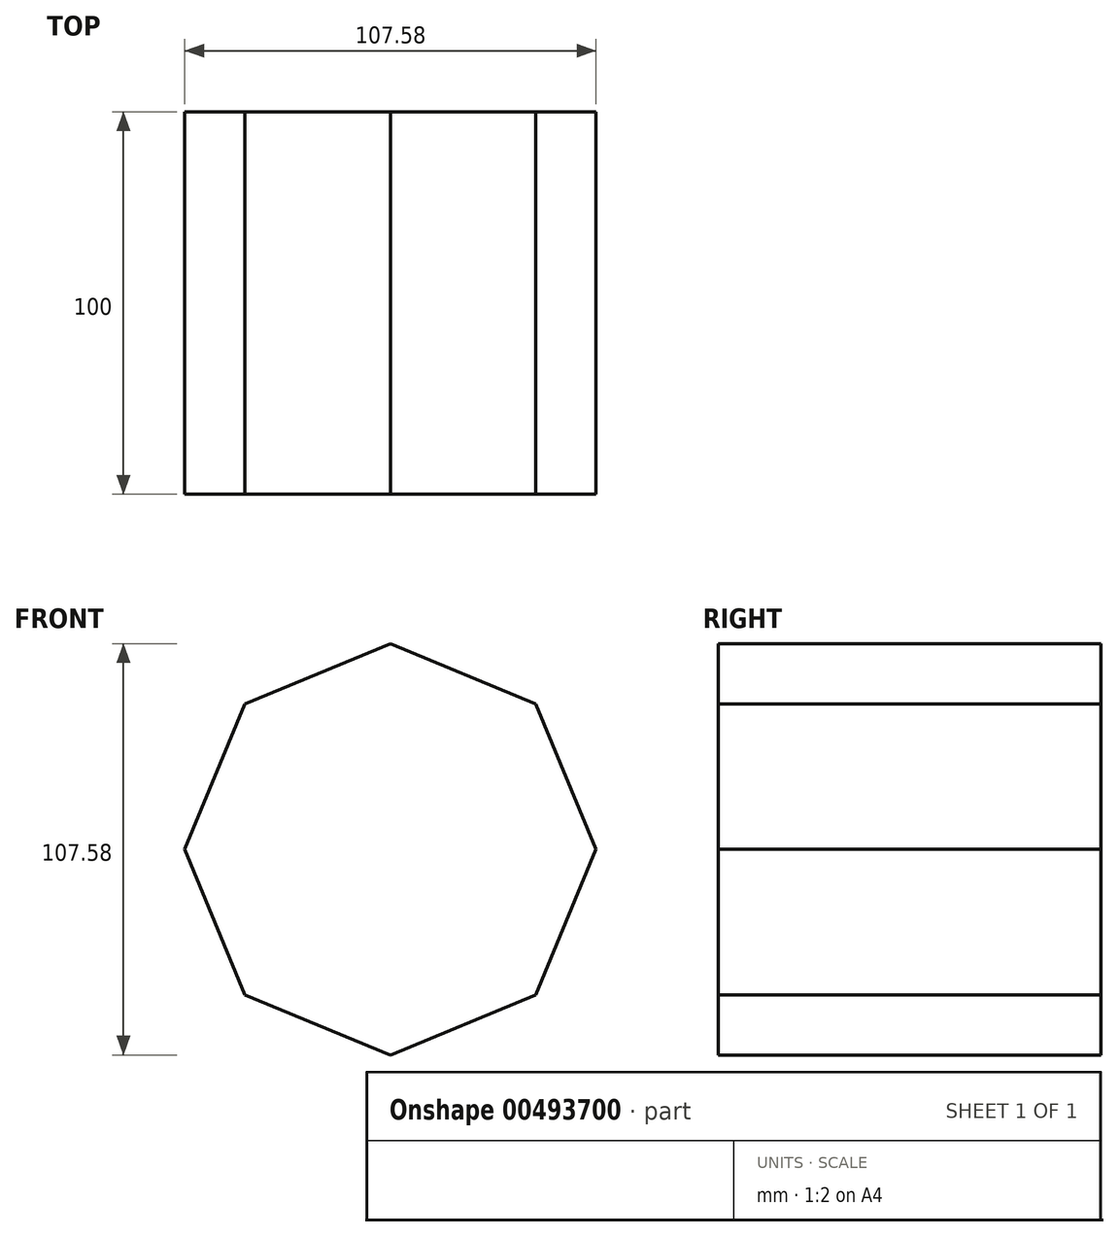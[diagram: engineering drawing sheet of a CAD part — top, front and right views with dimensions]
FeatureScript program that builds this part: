
annotation { "Feature Type Name" : "Feature", "Feature Type Description" : "" }
export const myFeature = defineFeature(function(context is Context, id is Id, definition is map)
    precondition{}
    {
        {
            var Q0;
            Q0=qCreatedBy(makeId("Front.planeOp"),FACE);
            var sketch = newSketch(context, id + "F0", { "sketchPlane" : qUnion([Q0])});
            skCircle(sketch, "E0.cCircle", {"center": v(0, 0) * mm, "radius": 53.8 * mm, "construction": true});
            skLineSegment(sketch, "E0.0", {"start": v(0, 53.8) * mm, "end": v(38.04, 38.04) * mm});
            skLineSegment(sketch, "E0.1", {"start": v(38.04, 38.04) * mm, "end": v(53.8, 0) * mm});
            skLineSegment(sketch, "E0.2", {"start": v(53.8, 0) * mm, "end": v(38.04, -38.04) * mm});
            skLineSegment(sketch, "E0.3", {"start": v(38.04, -38.04) * mm, "end": v(0, -53.8) * mm});
            skLineSegment(sketch, "E0.4", {"start": v(0, -53.8) * mm, "end": v(-38.04, -38.04) * mm});
            skLineSegment(sketch, "E0.5", {"start": v(-38.04, -38.04) * mm, "end": v(-53.8, 0) * mm});
            skLineSegment(sketch, "E0.6", {"start": v(-53.8, 0) * mm, "end": v(-38.04, 38.04) * mm});
            skLineSegment(sketch, "E0.7", {"start": v(-38.04, 38.04) * mm, "end": v(0, 53.8) * mm});
            skSolve(sketch);
        }
        {
            var Q0;
            Q0=makeQuery(id+"F0.imprint","IMPRINT",FACE,{"disambiguationData":[TD([[makeQuery(id+"F0.imprint","IMPRINT",EDGE,{"derivedFrom":sQuery(id+"F0.wireOp",EDGE,"E0.0")}),-1.0]])]});
            extrude(context, id + "F1", {"entities" : qUnion([Q0]), "depth" : 100 * mm});
        }
    });
